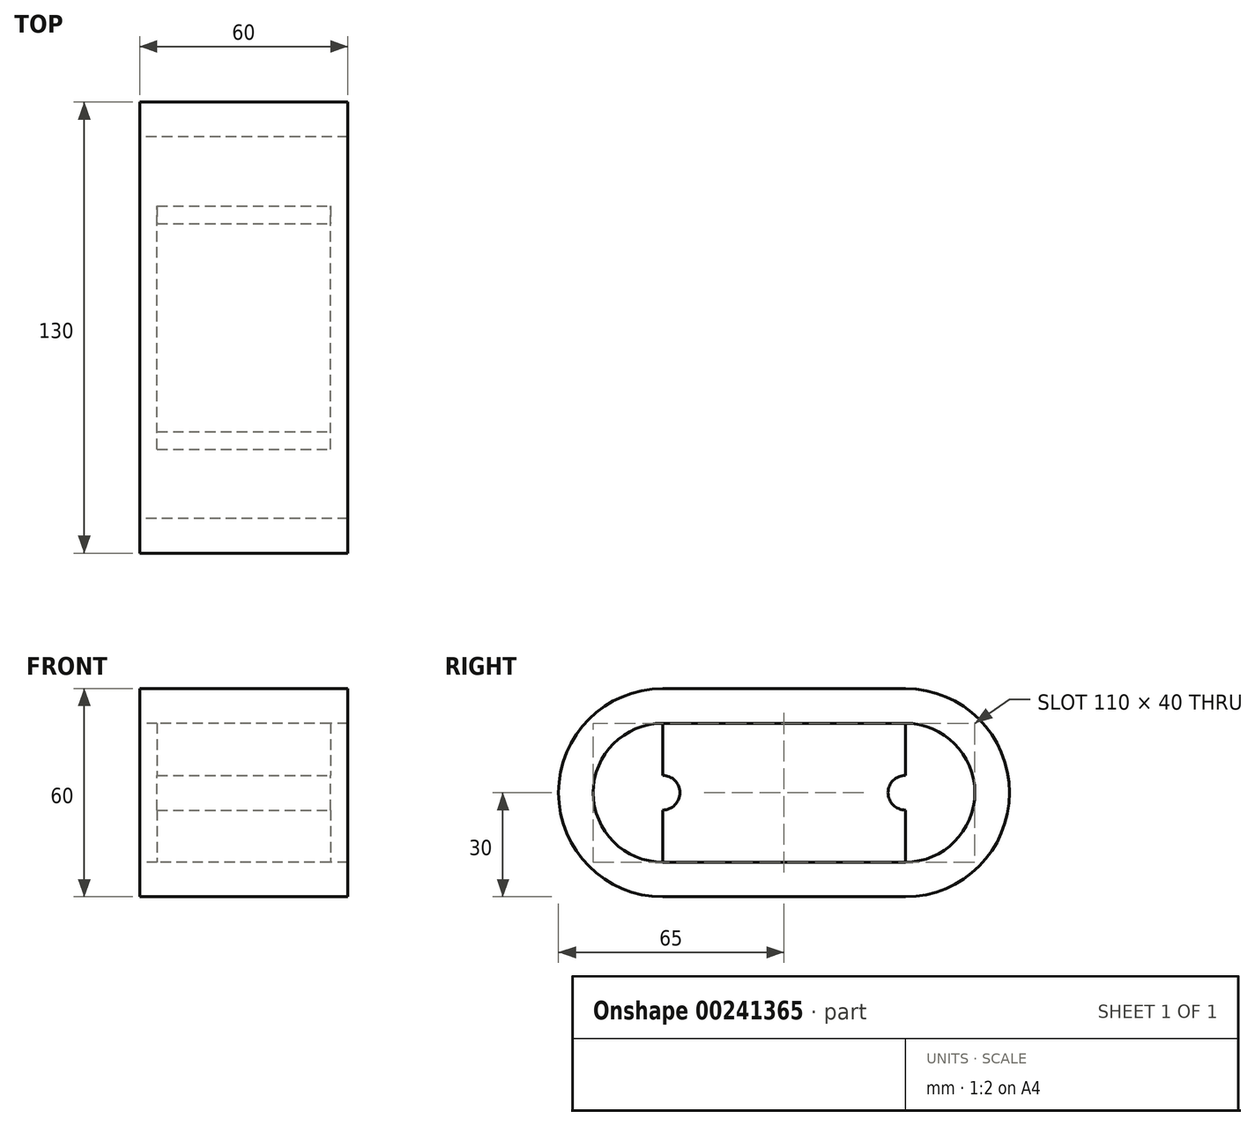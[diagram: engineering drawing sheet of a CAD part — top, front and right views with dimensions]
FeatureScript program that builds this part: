
annotation { "Feature Type Name" : "Feature", "Feature Type Description" : "" }
export const myFeature = defineFeature(function(context is Context, id is Id, definition is map)
    precondition{}
    {
        {
            var Q0;
            Q0=qCreatedBy(makeId("Right.planeOp"),FACE);
            var sketch = newSketch(context, id + "F0", { "sketchPlane" : qUnion([Q0])});
            skLineSegment(sketch, "E0.bottom", {"start": v(-35, 30) * mm, "end": v(35, 30) * mm});
            skLineSegment(sketch, "E0.top", {"start": v(-35, -30) * mm, "end": v(35, -30) * mm});
            skLineSegment(sketch, "E0.left", {"start": v(-35, 30) * mm, "end": v(-35, -30) * mm});
            skLineSegment(sketch, "E0.right", {"start": v(35, 30) * mm, "end": v(35, -30) * mm});
            skPoint(sketch, "E0.middle", {"position": v(0, 0) * mm});
            skLineSegment(sketch, "E1.bottom", {"start": v(-35, 20) * mm, "end": v(35, 20) * mm});
            skLineSegment(sketch, "E1.top", {"start": v(-35, -20) * mm, "end": v(35, -20) * mm});
            skLineSegment(sketch, "E1.left", {"start": v(-35, 20) * mm, "end": v(-35, -20) * mm});
            skLineSegment(sketch, "E1.right", {"start": v(35, 20) * mm, "end": v(35, -20) * mm});
            skArc(sketch, "E2", {"start": v(-35, 30) * mm, "mid": v(-65, 0) * mm, "end": v(-35, -30) * mm});
            skArc(sketch, "E3", {"start": v(-35, 20) * mm, "mid": v(-55, 0) * mm, "end": v(-35, -20) * mm});
            skArc(sketch, "E4", {"start": v(35, -30) * mm, "mid": v(65, 0) * mm, "end": v(35, 30) * mm});
            skArc(sketch, "E5", {"start": v(35, -20) * mm, "mid": v(55, 0) * mm, "end": v(35, 20) * mm});
            skSolve(sketch);
        }
        {
            var Q0;
            Q0 = qSketchRegion(id + "F0", true);
            extrude(context, id + "F1", {"entities" : qUnion([Q0]), "endBound" : BoundingType.SYMMETRIC, "depth" : 60 * mm});
        }
        {
            var Q0;
            Q0=makeQuery(id+"F0.imprint","IMPRINT",FACE,{"disambiguationData":[TD([[makeQuery(id+"F0.imprint","IMPRINT",EDGE,{"derivedFrom":sQuery(id+"F0.wireOp",EDGE,"E1.left")}),-1.0]])]});
            var Q1;
            Q1=makeQuery(id+"F0.imprint","IMPRINT",FACE,{"disambiguationData":[TD([[makeQuery(id+"F0.imprint","IMPRINT",EDGE,{"derivedFrom":sQuery(id+"F0.wireOp",EDGE,"E1.bottom")}),-1.0]])]});
            var Q2;
            Q2=makeQuery(id+"F0.imprint","IMPRINT",FACE,{"disambiguationData":[TD([[makeQuery(id+"F0.imprint","IMPRINT",EDGE,{"derivedFrom":sQuery(id+"F0.wireOp",EDGE,"E1.right")}),1.0]])]});
            extrude(context, id + "F2", {"entities" : qUnion([Q0, Q1, Q2]), "operationType" : NewBodyOperationType.ADD, "endBound" : BoundingType.SYMMETRIC, "depth" : 50 * mm});
        }
        {
            var Q0;
            Q0=makeQuery(id+"F2.opExtrude","CAP_FACE",FACE,{"disambiguationData":[OSD([sQuery(id+"F0.wireOp",EDGE,"E1.bottom"),sQuery(id+"F0.wireOp",EDGE,"E1.top"),sQuery(id+"F0.wireOp",EDGE,"E3"),sQuery(id+"F0.wireOp",EDGE,"E5")])],"isStart":false});
            var sketch = newSketch(context, id + "F3", { "sketchPlane" : qUnion([Q0])});
            skCircle(sketch, "E6", {"center": v(-35, 0) * mm, "radius": 5 * mm});
            skCircle(sketch, "E7", {"center": v(35, 0) * mm, "radius": 5 * mm});
            skSolve(sketch);
        }
        {
            var Q0;
            Q0 = qSketchRegion(id + "F3", true);
            extrude(context, id + "F4", {"entities" : qUnion([Q0]), "operationType" : NewBodyOperationType.REMOVE, "endBound" : BoundingType.THROUGH_ALL, "oppositeDirection" : true, "depth" : 25 * mm});
        }
    });
